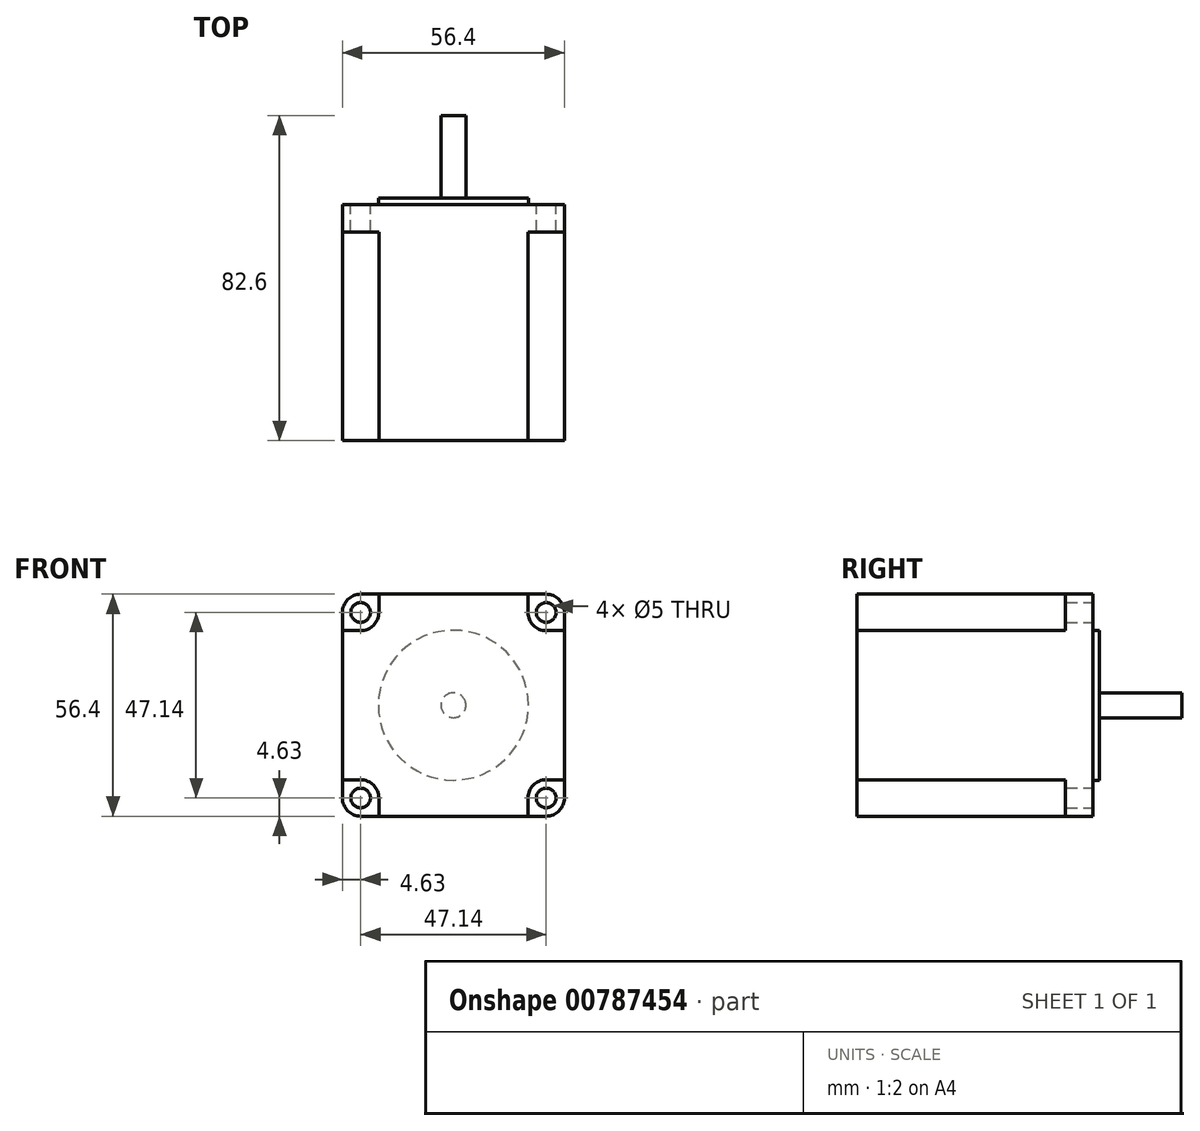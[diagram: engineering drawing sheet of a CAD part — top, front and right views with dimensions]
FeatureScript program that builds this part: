
annotation { "Feature Type Name" : "Feature", "Feature Type Description" : "" }
export const myFeature = defineFeature(function(context is Context, id is Id, definition is map)
    precondition{}
    {
        {
            var Q0;
            Q0=qCreatedBy(makeId("Front.planeOp"),FACE);
            var sketch = newSketch(context, id + "F0", { "sketchPlane" : qUnion([Q0])});
            skLineSegment(sketch, "E0.bottom", {"start": v(23.57, 28.2) * mm, "end": v(-23.57, 28.2) * mm});
            skLineSegment(sketch, "E0.top", {"start": v(23.57, -28.2) * mm, "end": v(-23.57, -28.2) * mm});
            skLineSegment(sketch, "E0.left", {"start": v(28.2, 23.57) * mm, "end": v(28.2, -23.57) * mm});
            skLineSegment(sketch, "E0.right", {"start": v(-28.2, 23.57) * mm, "end": v(-28.2, -23.57) * mm});
            skPoint(sketch, "E0.middle", {"position": v(0, 0) * mm});
            skCircle(sketch, "E1", {"center": v(-23.57, 23.57) * mm, "radius": 2.5 * mm});
            skCircle(sketch, "E2.MirrorC", {"center": v(23.57, 23.57) * mm, "radius": 2.5 * mm});
            skCircle(sketch, "E3.MirrorC", {"center": v(-23.57, -23.57) * mm, "radius": 2.5 * mm});
            skCircle(sketch, "E4.MirrorC", {"center": v(23.57, -23.57) * mm, "radius": 2.5 * mm});
            skPoint(sketch, "E5.visualSharp", {"position": v(-28.2, 28.2) * mm});
            skArc(sketch, "E5.filletArc", {"start": v(-23.57, 28.2) * mm, "mid": v(-26.84, 26.84) * mm, "end": v(-28.2, 23.57) * mm});
            skArc(sketch, "E6.MirrorCS", {"start": v(23.57, 28.2) * mm, "mid": v(26.84, 26.84) * mm, "end": v(28.2, 23.57) * mm});
            skArc(sketch, "E7.MirrorCS", {"start": v(-23.57, -28.2) * mm, "mid": v(-26.84, -26.84) * mm, "end": v(-28.2, -23.57) * mm});
            skArc(sketch, "E8.MirrorCS", {"start": v(23.57, -28.2) * mm, "mid": v(26.84, -26.84) * mm, "end": v(28.2, -23.57) * mm});
            skPoint(sketch, "E9.orphan", {"position": v(28.2, 28.2) * mm});
            skPoint(sketch, "E10.orphan", {"position": v(28.2, -28.2) * mm});
            skPoint(sketch, "E11.orphan", {"position": v(-28.2, -28.2) * mm});
            skSolve(sketch);
        }
        {
            var Q0;
            Q0=makeQuery(id+"F0.imprint","IMPRINT",FACE,{"disambiguationData":[TD([[makeQuery(id+"F0.imprint","IMPRINT",EDGE,{"derivedFrom":sQuery(id+"F0.wireOp",EDGE,"E0.bottom")}),1.0]])]});
            extrude(context, id + "F1", {"entities" : qUnion([Q0]), "depth" : 7 * mm, "offsetDistance" : 25 * mm});
        }
        {
            var Q0;
            Q0=makeQuery(id+"F1.opExtrude","CAP_FACE",FACE,{"disambiguationData":[OSD([sQuery(id+"F0.wireOp",EDGE,"E0.bottom"),sQuery(id+"F0.wireOp",EDGE,"E0.top"),sQuery(id+"F0.wireOp",EDGE,"E0.left"),sQuery(id+"F0.wireOp",EDGE,"E0.right"),sQuery(id+"F0.wireOp",EDGE,"E1"),sQuery(id+"F0.wireOp",EDGE,"E2.MirrorC"),sQuery(id+"F0.wireOp",EDGE,"E3.MirrorC"),sQuery(id+"F0.wireOp",EDGE,"E4.MirrorC"),sQuery(id+"F0.wireOp",EDGE,"E5.filletArc"),sQuery(id+"F0.wireOp",EDGE,"E6.MirrorCS"),sQuery(id+"F0.wireOp",EDGE,"E7.MirrorCS"),sQuery(id+"F0.wireOp",EDGE,"E8.MirrorCS")])],"isStart":false});
            var sketch = newSketch(context, id + "F2", { "sketchPlane" : qUnion([Q0])});
            skPoint(sketch, "E12.middle", {"position": v(0, 0) * mm});
            skLineSegment(sketch, "E13", {"start": v(-28.2, 0) * mm, "end": v(-28.2, 18.94) * mm});
            skLineSegment(sketch, "E14", {"start": v(-28.2, 18.94) * mm, "end": v(-23.57, 18.94) * mm});
            skLineSegment(sketch, "E15", {"start": v(-18.94, 23.57) * mm, "end": v(-18.94, 28.2) * mm});
            skLineSegment(sketch, "E16", {"start": v(-18.94, 28.2) * mm, "end": v(0, 28.2) * mm});
            skPoint(sketch, "E17.visualSharp", {"position": v(-18.94, 18.94) * mm});
            skArc(sketch, "E17.filletArc", {"start": v(-23.57, 18.94) * mm, "mid": v(-20.3, 20.3) * mm, "end": v(-18.94, 23.57) * mm});
            skLineSegment(sketch, "E18.MirrorCS", {"start": v(18.94, 28.2) * mm, "end": v(0, 28.2) * mm});
            skLineSegment(sketch, "E19.MirrorCS", {"start": v(18.94, 23.57) * mm, "end": v(18.94, 28.2) * mm});
            skArc(sketch, "E20.MirrorCS", {"start": v(23.57, 18.94) * mm, "mid": v(20.3, 20.3) * mm, "end": v(18.94, 23.57) * mm});
            skLineSegment(sketch, "E21.MirrorCS", {"start": v(28.2, 18.94) * mm, "end": v(23.57, 18.94) * mm});
            skLineSegment(sketch, "E22.MirrorCS", {"start": v(28.2, 0) * mm, "end": v(28.2, 18.94) * mm});
            skLineSegment(sketch, "E23.MirrorCS", {"start": v(-28.2, 0) * mm, "end": v(-28.2, -18.94) * mm});
            skLineSegment(sketch, "E24.MirrorCS", {"start": v(-28.2, -18.94) * mm, "end": v(-23.57, -18.94) * mm});
            skArc(sketch, "E25.MirrorCS", {"start": v(-23.57, -18.94) * mm, "mid": v(-20.3, -20.3) * mm, "end": v(-18.94, -23.57) * mm});
            skLineSegment(sketch, "E26.MirrorCS", {"start": v(-18.94, -23.57) * mm, "end": v(-18.94, -28.2) * mm});
            skLineSegment(sketch, "E27.MirrorCS", {"start": v(-18.94, -28.2) * mm, "end": v(0, -28.2) * mm});
            skLineSegment(sketch, "E28.MirrorCS", {"start": v(18.94, -28.2) * mm, "end": v(0, -28.2) * mm});
            skLineSegment(sketch, "E29.MirrorCS", {"start": v(18.94, -23.57) * mm, "end": v(18.94, -28.2) * mm});
            skArc(sketch, "E30.MirrorCS", {"start": v(23.57, -18.94) * mm, "mid": v(20.3, -20.3) * mm, "end": v(18.94, -23.57) * mm});
            skLineSegment(sketch, "E31.MirrorCS", {"start": v(28.2, -18.94) * mm, "end": v(23.57, -18.94) * mm});
            skLineSegment(sketch, "E32.MirrorCS", {"start": v(28.2, 0) * mm, "end": v(28.2, -18.94) * mm});
            skSolve(sketch);
        }
        {
            var Q0;
            Q0=makeQuery(id+"F2.imprint","IMPRINT",FACE,{"disambiguationData":[TD([[makeQuery(id+"F2.imprint","IMPRINT",EDGE,{"derivedFrom":sQuery(id+"F2.wireOp",EDGE,"E13")}),1.0]])]});
            extrude(context, id + "F3", {"entities" : qUnion([Q0]), "operationType" : NewBodyOperationType.ADD, "depth" : 53 * mm, "offsetDistance" : 25 * mm});
        }
        {
            var Q0;
            Q0=makeQuery(id+"F1.opExtrude","CAP_FACE",FACE,{"disambiguationData":[OSD([sQuery(id+"F0.wireOp",EDGE,"E0.bottom"),sQuery(id+"F0.wireOp",EDGE,"E0.top"),sQuery(id+"F0.wireOp",EDGE,"E0.left"),sQuery(id+"F0.wireOp",EDGE,"E0.right"),sQuery(id+"F0.wireOp",EDGE,"E1"),sQuery(id+"F0.wireOp",EDGE,"E2.MirrorC"),sQuery(id+"F0.wireOp",EDGE,"E3.MirrorC"),sQuery(id+"F0.wireOp",EDGE,"E4.MirrorC"),sQuery(id+"F0.wireOp",EDGE,"E5.filletArc"),sQuery(id+"F0.wireOp",EDGE,"E6.MirrorCS"),sQuery(id+"F0.wireOp",EDGE,"E7.MirrorCS"),sQuery(id+"F0.wireOp",EDGE,"E8.MirrorCS")])],"isStart":true});
            var sketch = newSketch(context, id + "F4", { "sketchPlane" : qUnion([Q0])});
            skCircle(sketch, "E33", {"center": v(0, 0) * mm, "radius": 19.05 * mm});
            skSolve(sketch);
        }
        {
            var Q0;
            Q0=makeQuery(id+"F4.imprint","IMPRINT",FACE,{"disambiguationData":[TD([[makeQuery(id+"F4.imprint","IMPRINT",EDGE,{"derivedFrom":sQuery(id+"F4.wireOp",EDGE,"E33")}),1.0]])]});
            extrude(context, id + "F5", {"entities" : qUnion([Q0]), "operationType" : NewBodyOperationType.ADD, "depth" : 1.6 * mm, "offsetDistance" : 25 * mm});
        }
        {
            var Q0;
            Q0=makeQuery(id+"F5.opExtrude","CAP_FACE",FACE,{"disambiguationData":[OSD([sQuery(id+"F4.wireOp",EDGE,"E33")])],"isStart":false});
            var sketch = newSketch(context, id + "F6", { "sketchPlane" : qUnion([Q0])});
            skCircle(sketch, "E34", {"center": v(0, 0) * mm, "radius": 3.18 * mm});
            skSolve(sketch);
        }
        {
            var Q0;
            Q0=makeQuery(id+"F6.imprint","IMPRINT",FACE,{"disambiguationData":[TD([[makeQuery(id+"F6.imprint","IMPRINT",EDGE,{"derivedFrom":sQuery(id+"F6.wireOp",EDGE,"E34")}),1.0]])]});
            extrude(context, id + "F7", {"entities" : qUnion([Q0]), "operationType" : NewBodyOperationType.ADD, "depth" : 21 * mm, "offsetDistance" : 25 * mm});
        }
    });
